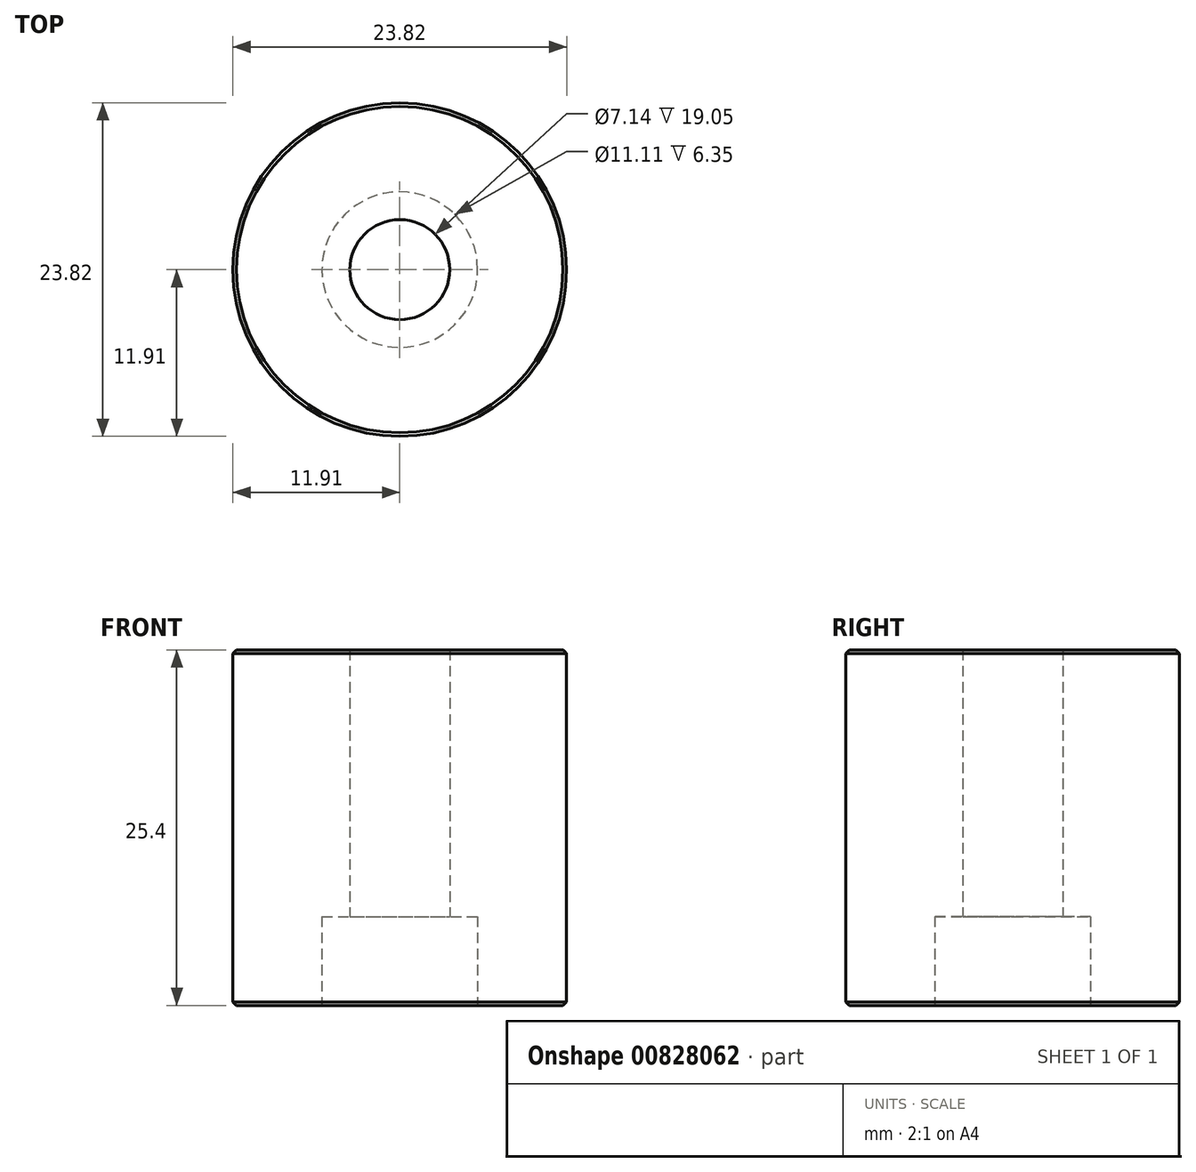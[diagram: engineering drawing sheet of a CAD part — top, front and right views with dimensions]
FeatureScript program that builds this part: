
annotation { "Feature Type Name" : "Feature", "Feature Type Description" : "" }
export const myFeature = defineFeature(function(context is Context, id is Id, definition is map)
    precondition{}
    {
        {
            var Q0;
            Q0=qCreatedBy(makeId("Top.planeOp"),FACE);
            var sketch = newSketch(context, id + "F0", { "sketchPlane" : qUnion([Q0])});
            skCircle(sketch, "E0", {"center": v(0, 0) * mm, "radius": 11.9 * mm});
            skSolve(sketch);
        }
        {
            var Q0;
            Q0 = qSketchRegion(id + "F0", true);
            extrude(context, id + "F1", {"entities" : qUnion([Q0]), "depth" : 25.4 * mm, "offsetDistance" : 25.4 * mm});
        }
        {
            var Q0;
            Q0=sQuery(id+"F0.wireOp",VERTEX,"E0.center");
            var Q1;
            Q1=makeQuery(id+"F1.opExtrude","SWEPT_BODY",BODY,{"disambiguationData":[OSD([sQuery(id+"F0.wireOp",EDGE,"E0")])]});
            hole(context, id + "F2", {"style" : HoleStyle.C_BORE, "endStyle" : HoleEndStyle.THROUGH, "oppositeDirection" : true, "holeDiameter" : 7.14 * mm, "cBoreDiameter" : 11.1 * mm, "cBoreDepth" : 6.35 * mm, "majorDiameter" : 6.35 * mm, "isTappedThrough" : true, "tappedDepth" : 12.7 * mm, "tapClearance" : 3, "locations" : qUnion([Q0]), "scope" : qUnion([Q1])});
        }
        {
            var Q0;
            Q0=makeQuery(id+"F1.opExtrude","CAP_EDGE",EDGE,{"disambiguationData":[OSD([sQuery(id+"F0.wireOp",EDGE,"E0")])],"isStart":false});
            var Q1;
            Q1=makeQuery(id+"F2.hole-0.boolean.opBoolean","INTERSECT",EDGE,{"derivedFrom":[makeQuery(id+"F1.opExtrude","CAP_FACE",FACE,{"disambiguationData":[OSD([sQuery(id+"F0.wireOp",EDGE,"E0")])],"isStart":false}),makeQuery(id+"F2.hole-0.opRevolve","SWEPT_FACE",FACE,{"disambiguationData":[OSD([sQuery(id+"F2.hole-0.sketch.wireOp",EDGE,"core_line_2")])]})]});
            var Q2;
            Q2=makeQuery(id+"F1.opExtrude","CAP_EDGE",EDGE,{"disambiguationData":[OSD([sQuery(id+"F0.wireOp",EDGE,"E0")])],"isStart":true});
            var Q3;
            Q3=makeQuery(id+"F2.hole-0.boolean.opBoolean","COPY",EDGE,{"derivedFrom":makeQuery(id+"F2.hole-0.opRevolve","SWEPT_EDGE",EDGE,{"disambiguationData":[OSD([sQuery(id+"F2.hole-0.sketch.wireOp",EDGE,"cbore_start_line_2"),sQuery(id+"F2.hole-0.sketch.wireOp",EDGE,"cbore_start_line_3")])]})});
            chamfer(context, id + "F3", {"entities" : qUnion([Q0, Q1, Q2, Q3]), "width" : 0.25 * mm, "tangentPropagation" : true});
        }
    });
